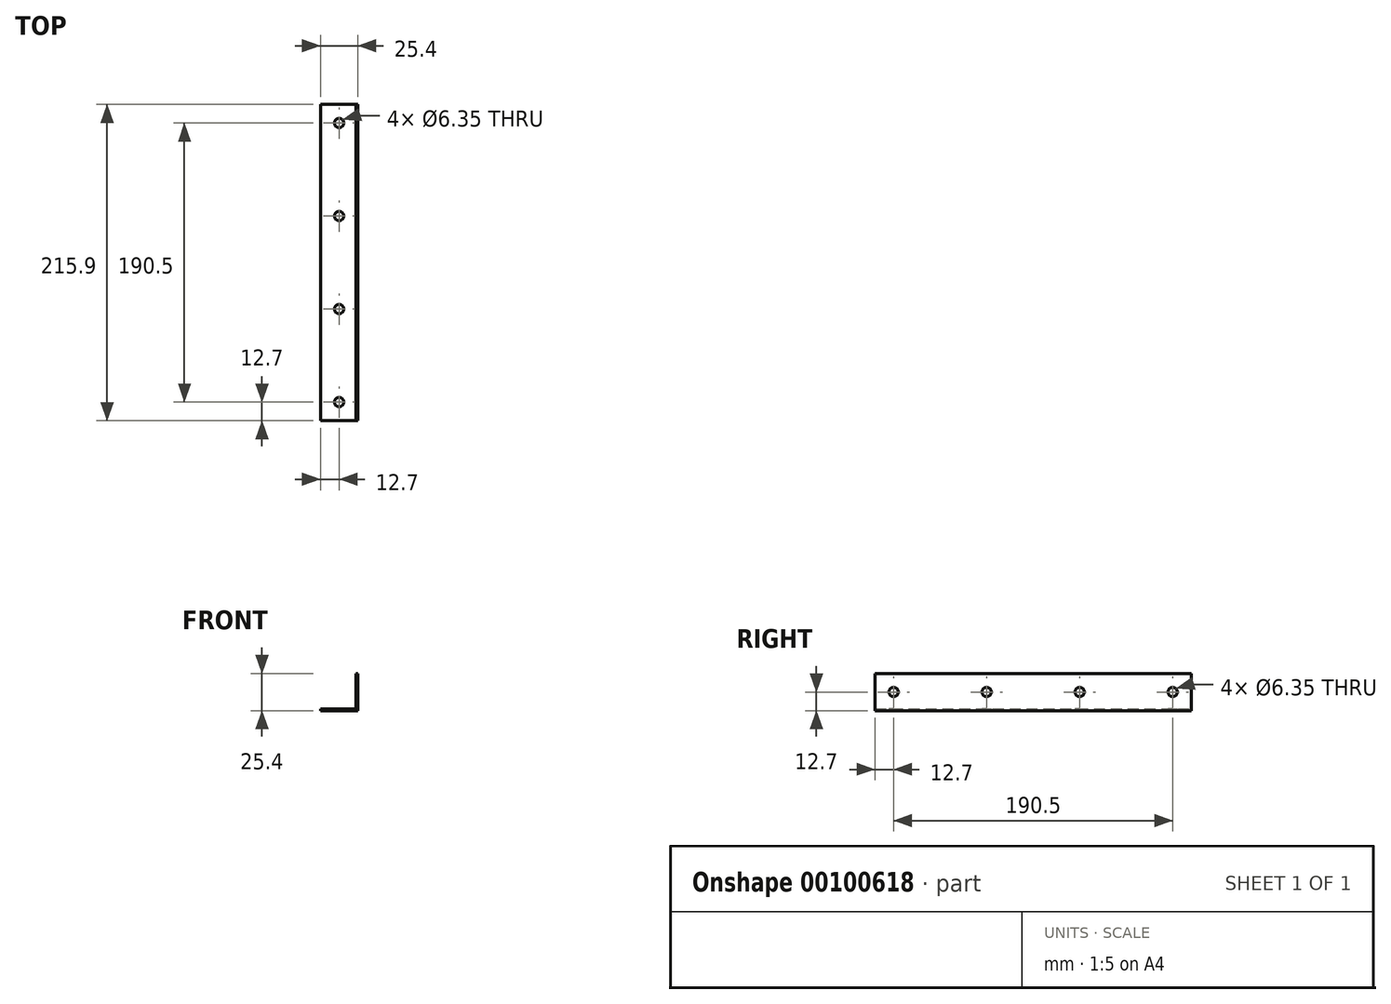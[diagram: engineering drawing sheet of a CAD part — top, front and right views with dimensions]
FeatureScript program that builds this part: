
annotation { "Feature Type Name" : "Feature", "Feature Type Description" : "" }
export const myFeature = defineFeature(function(context is Context, id is Id, definition is map)
    precondition{}
    {
        {
            var Q0;
            Q0=qCreatedBy(makeId("Front.planeOp"),FACE);
            var sketch = newSketch(context, id + "F0", { "sketchPlane" : qUnion([Q0])});
            skLineSegment(sketch, "E0", {"start": v(-12.7, -12.7) * mm, "end": v(12.7, -12.7) * mm});
            skLineSegment(sketch, "E1", {"start": v(12.7, -12.7) * mm, "end": v(12.7, 12.7) * mm});
            skPoint(sketch, "E2", {"position": v(0, -12.7) * mm});
            skLineSegment(sketch, "E3.0", {"start": v(11.43, -11.43) * mm, "end": v(11.43, 12.7) * mm});
            skLineSegment(sketch, "E3.1", {"start": v(-12.7, -11.43) * mm, "end": v(11.43, -11.43) * mm});
            skLineSegment(sketch, "E4", {"start": v(-12.7, -12.7) * mm, "end": v(-12.7, -11.43) * mm});
            skLineSegment(sketch, "E5", {"start": v(11.43, 12.7) * mm, "end": v(12.7, 12.7) * mm});
            skSolve(sketch);
        }
        {
            var Q0;
            Q0 = qSketchRegion(id + "F0", true);
            extrude(context, id + "F1", {"entities" : qUnion([Q0]), "depth" : 215.9 * mm});
        }
        {
            var Q0;
            Q0=makeQuery(id+"F1.opExtrude","SWEPT_FACE",FACE,{"disambiguationData":[OSD([sQuery(id+"F0.wireOp",EDGE,"E0")])]});
            var sketch = newSketch(context, id + "F2", { "sketchPlane" : qUnion([Q0])});
            skCircle(sketch, "E6", {"center": v(0, 203.2) * mm, "radius": 3.18 * mm});
            skCircle(sketch, "E7", {"center": v(0, 139.7) * mm, "radius": 3.18 * mm});
            skLineSegment(sketch, "E8", {"start": v(12.7, 107.95) * mm, "end": v(-12.7, 107.95) * mm, "construction": true});
            skCircle(sketch, "E9.MirrorC", {"center": v(0, 76.2) * mm, "radius": 3.18 * mm});
            skCircle(sketch, "E10.MirrorC", {"center": v(0, 12.7) * mm, "radius": 3.18 * mm});
            skSolve(sketch);
        }
        {
            var Q0;
            Q0 = qSketchRegion(id + "F2", true);
            extrude(context, id + "F3", {"entities" : qUnion([Q0]), "operationType" : NewBodyOperationType.REMOVE, "endBound" : BoundingType.THROUGH_ALL, "oppositeDirection" : true, "depth" : 25.4 * mm});
        }
        {
            var Q0;
            Q0=makeQuery(id+"F1.opExtrude","SWEPT_FACE",FACE,{"disambiguationData":[OSD([sQuery(id+"F0.wireOp",EDGE,"E1")])]});
            var sketch = newSketch(context, id + "F4", { "sketchPlane" : qUnion([Q0])});
            skPoint(sketch, "E11.centerSnap0", {"position": v(0, 0) * mm});
            skCircle(sketch, "E12", {"center": v(-139.7, 0) * mm, "radius": 3.18 * mm});
            skCircle(sketch, "E13", {"center": v(-203.2, 0) * mm, "radius": 3.18 * mm});
            skPoint(sketch, "E13.centerSnap0", {"position": v(-215.9, 0) * mm});
            skLineSegment(sketch, "E14", {"start": v(-107.95, 12.7) * mm, "end": v(-107.95, -12.7) * mm, "construction": true});
            skCircle(sketch, "E15.MirrorC", {"center": v(-76.2, 0) * mm, "radius": 3.18 * mm});
            skCircle(sketch, "E16.MirrorC", {"center": v(-12.7, 0) * mm, "radius": 3.18 * mm});
            skSolve(sketch);
        }
        {
            var Q0;
            Q0 = qSketchRegion(id + "F4", true);
            extrude(context, id + "F5", {"entities" : qUnion([Q0]), "operationType" : NewBodyOperationType.REMOVE, "oppositeDirection" : true, "depth" : 25.4 * mm});
        }
    });
